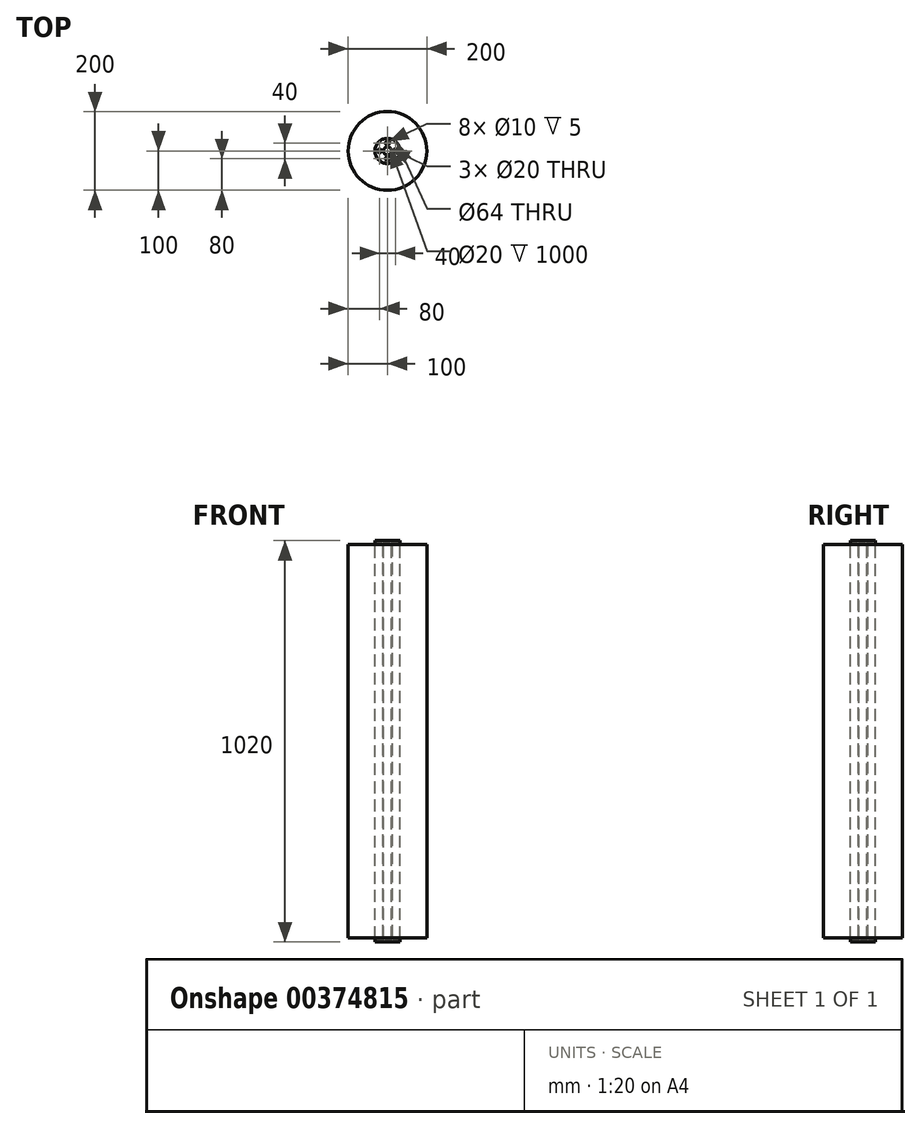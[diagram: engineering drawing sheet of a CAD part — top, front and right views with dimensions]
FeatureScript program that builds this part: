
annotation { "Feature Type Name" : "Feature", "Feature Type Description" : "" }
export const myFeature = defineFeature(function(context is Context, id is Id, definition is map)
    precondition{}
    {
        {
            var Q0;
            Q0=qCreatedBy(makeId("Top.planeOp"),FACE);
            var sketch = newSketch(context, id + "F0", { "sketchPlane" : qUnion([Q0])});
            skCircle(sketch, "E0", {"center": v(0, 0) * mm, "radius": 10 * mm});
            skCircle(sketch, "E1", {"center": v(0, 0) * mm, "radius": 12 * mm});
            skSolve(sketch);
        }
        {
            var Q0;
            Q0=makeQuery(id+"F0.imprint","IMPRINT",FACE,{"disambiguationData":[TD([[makeQuery(id+"F0.imprint","IMPRINT",EDGE,{"derivedFrom":sQuery(id+"F0.wireOp",EDGE,"E0")}),-1.0]])]});
            extrude(context, id + "F1", {"entities" : qUnion([Q0]), "depth" : 1000 * mm});
        }
        {
            var Q0;
            Q0=makeQuery(id+"F1.opExtrude","CAP_FACE",FACE,{"disambiguationData":[OSD([sQuery(id+"F0.wireOp",EDGE,"E0"),sQuery(id+"F0.wireOp",EDGE,"E1")])],"isStart":false});
            var sketch = newSketch(context, id + "F2", { "sketchPlane" : qUnion([Q0])});
            skCircle(sketch, "E2", {"center": v(0, 0) * mm, "radius": 32 * mm});
            skSolve(sketch);
        }
        {
            var Q0;
            Q0=makeQuery(id+"F2.imprint","IMPRINT",FACE,{"disambiguationData":[TD([[makeQuery(id+"F2.imprint","IMPRINT",EDGE,{"derivedFrom":sQuery(id+"F2.wireOp",EDGE,"E2")}),1.0]])]});
            var Q1;
            Q1=makeQuery(id+"F2.imprint","IMPRINT",FACE,{"disambiguationData":[TD([[makeQuery(id+"F2.imprint","IMPRINT",EDGE,{"derivedFrom":makeQuery(id+"F1.opExtrude","CAP_EDGE",EDGE,{"disambiguationData":[OSD([sQuery(id+"F0.wireOp",EDGE,"E0")])],"isStart":false})}),-1.0]])]});
            extrude(context, id + "F3", {"entities" : qUnion([Q0, Q1]), "depth" : 10 * mm});
        }
        {
            var Q0;
            Q0=makeQuery(id+"F1.opExtrude","CAP_FACE",FACE,{"disambiguationData":[OSD([sQuery(id+"F0.wireOp",EDGE,"E0"),sQuery(id+"F0.wireOp",EDGE,"E1")])],"isStart":true});
            var sketch = newSketch(context, id + "F4", { "sketchPlane" : qUnion([Q0])});
            skCircle(sketch, "E3", {"center": v(0, 0) * mm, "radius": 32 * mm});
            skSolve(sketch);
        }
        {
            var Q0;
            Q0=makeQuery(id+"F4.imprint","IMPRINT",FACE,{"disambiguationData":[TD([[makeQuery(id+"F4.imprint","IMPRINT",EDGE,{"derivedFrom":makeQuery(id+"F1.opExtrude","CAP_EDGE",EDGE,{"disambiguationData":[OSD([sQuery(id+"F0.wireOp",EDGE,"E0")])],"isStart":true})}),1.0]])]});
            var Q1;
            Q1=makeQuery(id+"F4.imprint","IMPRINT",FACE,{"disambiguationData":[TD([[makeQuery(id+"F4.imprint","IMPRINT",EDGE,{"derivedFrom":sQuery(id+"F4.wireOp",EDGE,"E3")}),1.0]])]});
            extrude(context, id + "F5", {"entities" : qUnion([Q0, Q1]), "depth" : 10 * mm});
        }
        {
            var Q0;
            Q0=makeQuery(id+"F3.opExtrude","CAP_FACE",FACE,{"disambiguationData":[OSD([sQuery(id+"F0.wireOp",EDGE,"E0"),sQuery(id+"F2.wireOp",EDGE,"E2")])],"isStart":true});
            var Q1;
            Q1=makeQuery(id+"F5.opExtrude","CAP_FACE",FACE,{"disambiguationData":[OSD([sQuery(id+"F0.wireOp",EDGE,"E0"),sQuery(id+"F4.wireOp",EDGE,"E3")])],"isStart":true});
            extrude(context, id + "F6", {"entities" : qUnion([Q0]), "endBound" : BoundingType.UP_TO_SURFACE, "endBoundEntityFace" : qUnion([Q1]), "depth" : 25 * mm});
        }
        {
            var Q0;
            Q0=makeQuery(id+"F5.opExtrude","CAP_FACE",FACE,{"disambiguationData":[OSD([sQuery(id+"F0.wireOp",EDGE,"E0"),sQuery(id+"F4.wireOp",EDGE,"E3")])],"isStart":false});
            var sketch = newSketch(context, id + "F7", { "sketchPlane" : qUnion([Q0])});
            skCircle(sketch, "E4", {"center": v(0, 20) * mm, "radius": 5 * mm});
            skCircle(sketch, "E5.1.0", {"center": v(-20, 0) * mm, "radius": 5 * mm});
            skCircle(sketch, "E5.2.0", {"center": v(0, -20) * mm, "radius": 5 * mm});
            skPoint(sketch, "E5.center", {"position": v(0, 0) * mm});
            skCircle(sketch, "E6.1.3.0", {"center": v(20, 0) * mm, "radius": 5 * mm});
            skSolve(sketch);
        }
        {
            var Q0;
            Q0 = qSketchRegion(id + "F7", true);
            extrude(context, id + "F8", {"entities" : qUnion([Q0]), "operationType" : NewBodyOperationType.REMOVE, "oppositeDirection" : true, "depth" : 5 * mm});
        }
        {
            var Q0;
            Q0=makeQuery(id+"F3.opExtrude","CAP_FACE",FACE,{"disambiguationData":[OSD([sQuery(id+"F0.wireOp",EDGE,"E0"),sQuery(id+"F2.wireOp",EDGE,"E2")])],"isStart":false});
            var sketch = newSketch(context, id + "F9", { "sketchPlane" : qUnion([Q0])});
            skCircle(sketch, "E7", {"center": v(0, 20) * mm, "radius": 5 * mm});
            skCircle(sketch, "E8.1.0", {"center": v(-20, 0) * mm, "radius": 5 * mm});
            skCircle(sketch, "E8.2.0", {"center": v(0, -20) * mm, "radius": 5 * mm});
            skPoint(sketch, "E8.center", {"position": v(0, 0) * mm});
            skCircle(sketch, "E9.1.3.0", {"center": v(20, 0) * mm, "radius": 5 * mm});
            skSolve(sketch);
        }
        {
            var Q0;
            Q0 = qSketchRegion(id + "F9", true);
            extrude(context, id + "F10", {"entities" : qUnion([Q0]), "operationType" : NewBodyOperationType.REMOVE, "oppositeDirection" : true, "depth" : 5 * mm});
        }
        {
            var Q0;
            Q0=makeQuery(id+"F3.opExtrude","CAP_FACE",FACE,{"disambiguationData":[OSD([sQuery(id+"F0.wireOp",EDGE,"E0"),sQuery(id+"F2.wireOp",EDGE,"E2")])],"isStart":true});
            var sketch = newSketch(context, id + "F11", { "sketchPlane" : qUnion([Q0])});
            skCircle(sketch, "E10", {"center": v(0, 0) * mm, "radius": 100 * mm});
            skSolve(sketch);
        }
        {
            var Q0;
            Q0=makeQuery(id+"F11.imprint","IMPRINT",FACE,{"disambiguationData":[TD([[makeQuery(id+"F11.imprint","IMPRINT",EDGE,{"derivedFrom":sQuery(id+"F11.wireOp",EDGE,"E10")}),1.0]])]});
            var Q1;
            Q1=makeQuery(id+"F5.opExtrude","CAP_FACE",FACE,{"disambiguationData":[OSD([sQuery(id+"F0.wireOp",EDGE,"E0"),sQuery(id+"F4.wireOp",EDGE,"E3")])],"isStart":true});
            extrude(context, id + "F12", {"entities" : qUnion([Q0]), "endBound" : BoundingType.UP_TO_SURFACE, "endBoundEntityFace" : qUnion([Q1]), "depth" : 25 * mm});
        }
    });
